# Revit family: Micro Flood-EL218
name_source: partatom
category: Lighting Fixtures
units: mm (PartAtom-declared; Revit-internal decimal feet)

## family parameters
Cut with Voids When Loaded = No
Host = Face
Light Source = No
OmniClass Number = 23.80.70.14.14
OmniClass Title = Exterior Floodlights
Part Type = Normal
Room Calculation Point = No
Round Connector Dimension = Use Diameter
Shared = Yes

## types (1)
- EL218
    Angle = 0.00°
    Apparent Load = 0 VA
    Assembly Code = D5020200
    Cost = 0 $
    Default Elevation = 0' - 0"
    Description = Exterior Lighting
    Distribution = Wide Flood
    Drive Current = 550mA, 16W
    Full Load Current = 0 A
    Glass Material = Glass-Clear
    Lamp = 8 LED's
    Load Classification = Lighting
    Manufacturer = Kim Lighting
    MasterFormat Title = Flood Lighting
    Model = EL218
    Note Text = LF
    Note Visible = Yes
    Number of Poles = 1
    OmniClass Number = 23-80 70 14 14
    OmniClass Title = Exterior Floodlighting
    Outside Material = Dark Bronze
    Power Factor = 0.9
    Series = Micro Flood
    Type Comments = Lighting Fixture
    URL = https://www.currentlighting.com
    Voltage = 120 V
    Watts = 16 W

## geometry (parser evidence)
native form markers: Blend x10, Sweep x6
no freeform markers — native parametric forms only
